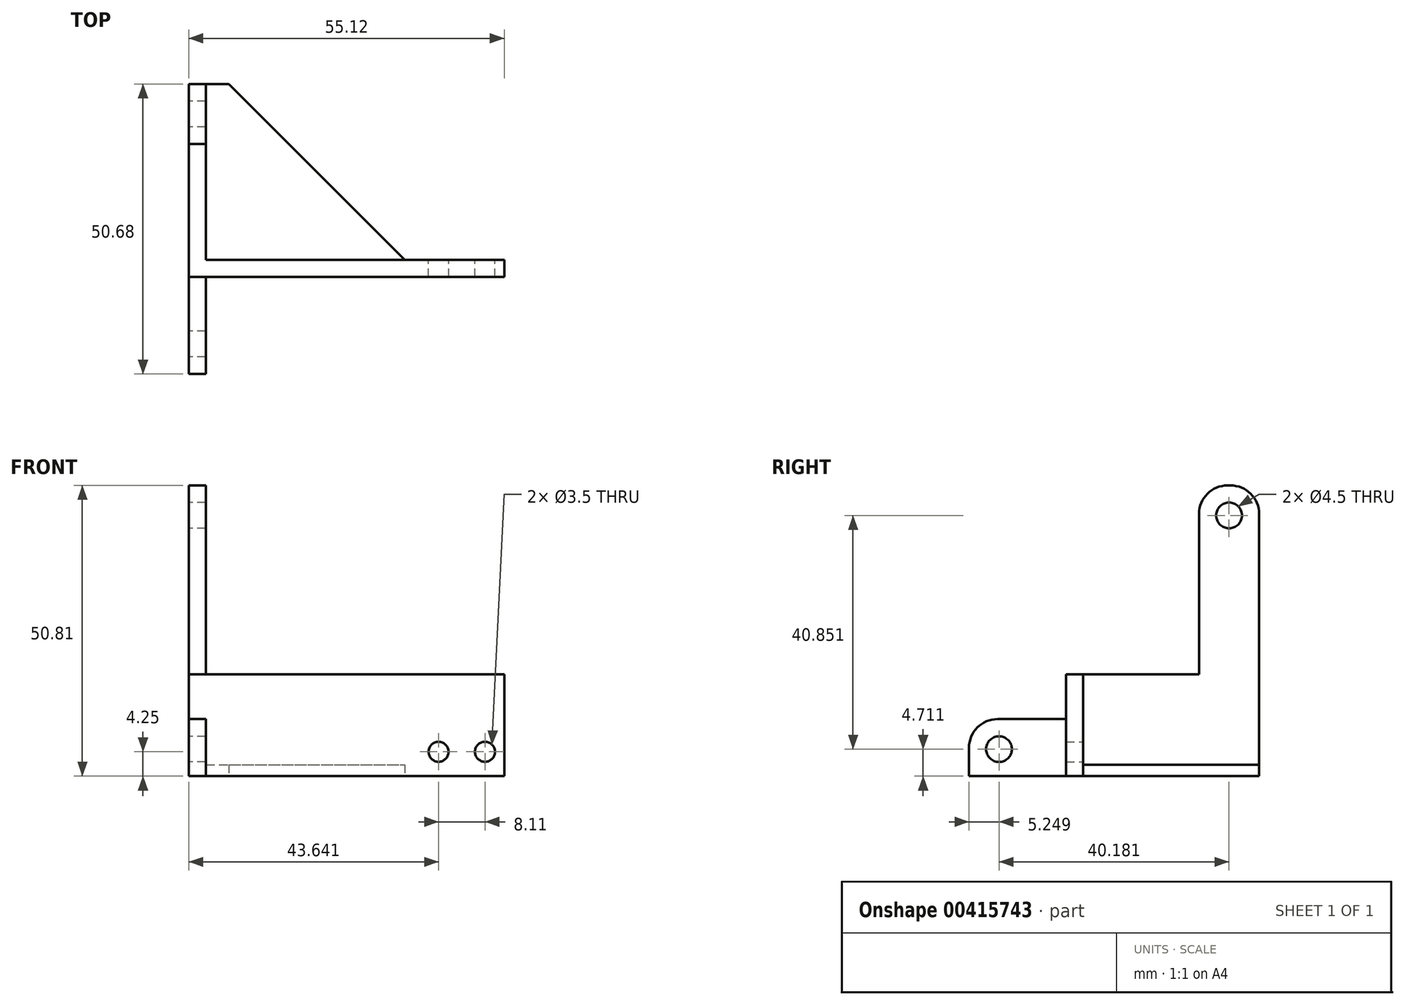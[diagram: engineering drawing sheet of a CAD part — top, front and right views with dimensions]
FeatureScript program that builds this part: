
annotation { "Feature Type Name" : "Feature", "Feature Type Description" : "" }
export const myFeature = defineFeature(function(context is Context, id is Id, definition is map)
    precondition{}
    {
        {
            var Q0;
            Q0=qCreatedBy(makeId("Front.planeOp"),FACE);
            var sketch = newSketch(context, id + "F0", { "sketchPlane" : qUnion([Q0])});
            skLineSegment(sketch, "E0.bottom", {"start": v(-7.56, 8.88) * mm, "end": v(7.56, 8.88) * mm});
            skLineSegment(sketch, "E0.top", {"start": v(-7.56, -8.88) * mm, "end": v(7.56, -8.88) * mm});
            skLineSegment(sketch, "E0.left", {"start": v(-7.56, 8.88) * mm, "end": v(-7.56, -8.88) * mm});
            skLineSegment(sketch, "E0.right", {"start": v(7.56, 8.88) * mm, "end": v(7.56, -8.88) * mm});
            skCircle(sketch, "E1", {"center": v(-3.92, -4.63) * mm, "radius": 1.75 * mm});
            skCircle(sketch, "E2", {"center": v(4.2, -4.63) * mm, "radius": 1.75 * mm});
            skLineSegment(sketch, "E3.bottom", {"start": v(-7.56, 8.88) * mm, "end": v(-47.56, 8.88) * mm});
            skLineSegment(sketch, "E3.top", {"start": v(-7.56, -8.88) * mm, "end": v(-47.56, -8.88) * mm});
            skLineSegment(sketch, "E3.right", {"start": v(-47.56, 8.88) * mm, "end": v(-47.56, -8.88) * mm});
            skLineSegment(sketch, "E4", {"start": v(-44.56, 8.88) * mm, "end": v(-44.56, -8.88) * mm});
            skLineSegment(sketch, "E5", {"start": v(-47.56, -6.88) * mm, "end": v(-9.56, -6.88) * mm});
            skLineSegment(sketch, "E6", {"start": v(-9.56, -6.88) * mm, "end": v(-9.56, -8.88) * mm});
            skSolve(sketch);
        }
        {
            var Q0;
            Q0=makeQuery(id+"F0.imprint","IMPRINT",FACE,{"disambiguationData":[TD([[makeQuery(id+"F0.imprint","IMPRINT",EDGE,{"derivedFrom":sQuery(id+"F0.wireOp",EDGE,"E0.bottom")}),-1.0]])]});
            var Q1;
            Q1=makeQuery(id+"F0.imprint","IMPRINT",FACE,{"disambiguationData":[TD([[makeQuery(id+"F0.imprint","IMPRINT",EDGE,{"derivedFrom":sQuery(id+"F0.wireOp",EDGE,"E3.bottom")}),1.0]])]});
            var Q2;
            {var subQ5=sQuery(id+"F0.wireOp",EDGE,"E0.left");Q2=makeQuery(id+"F0.imprint","IMPRINT",FACE,{"disambiguationData":[TD([[makeQuery(id+"F0.imprint","IMPRINT",EDGE,{"derivedFrom":subQ5}),-1.0]])]});}
            var Q3;
            {var subQ3=sQuery(id+"F0.wireOp",EDGE,"E6");Q3=makeQuery(id+"F0.imprint","IMPRINT",FACE,{"disambiguationData":[TD([[makeQuery(id+"F0.imprint","IMPRINT",EDGE,{"derivedFrom":subQ3}),-1.0]])]});}
            var Q4;
            {var subQ0=sQuery(id+"F0.wireOp",EDGE,"E3.right");var subQ1=sQuery(id+"F0.wireOp",EDGE,"E3.top");var subQ2=makeQuery(id+"F0.imprint","INTERSECT",VERTEX,{"derivedFrom":[subQ1,subQ0]});Q4=makeQuery(id+"F0.imprint","IMPRINT",FACE,{"disambiguationData":[TD([[makeQuery(id+"F0.imprint","IMPRINT",EDGE,{"disambiguationData":[TD([[subQ2,1.0]])],"derivedFrom":subQ1}),-1.0]])]});}
            extrude(context, id + "F1", {"entities" : qUnion([Q0, Q1, Q2, Q3, Q4]), "depth" : 3 * mm});
        }
        {
            var Q0;
            {var subQ0=sQuery(id+"F0.wireOp",EDGE,"E3.right");Q0=makeQuery(id+"F0.imprint","IMPRINT",FACE,{"disambiguationData":[TD([[makeQuery(id+"F0.imprint","IMPRINT",EDGE,{"derivedFrom":subQ0}),1.0]])]});}
            var Q1;
            {var subQ3=sQuery(id+"F0.wireOp",EDGE,"E6");Q1=makeQuery(id+"F0.imprint","IMPRINT",FACE,{"disambiguationData":[TD([[makeQuery(id+"F0.imprint","IMPRINT",EDGE,{"derivedFrom":subQ3}),-1.0]])]});}
            extrude(context, id + "F2", {"entities" : qUnion([Q0, Q1]), "operationType" : NewBodyOperationType.ADD, "oppositeDirection" : true, "depth" : 30.75 * mm});
        }
        {
            var Q0;
            {var subQ0=sQuery(id+"F0.wireOp",EDGE,"E3.right");Q0=makeQuery(id+"F2.boolean.opBoolean","MERGE",FACE,{"derivedFrom":[makeQuery(id+"F1.opExtrude","SWEPT_FACE",FACE,{"disambiguationData":[OSD([subQ0])]}),makeQuery(id+"F2.opExtrude","SWEPT_FACE",FACE,{"disambiguationData":[OSD([subQ0])]})]});}
            var sketch = newSketch(context, id + "F3", { "sketchPlane" : qUnion([Q0])});
            skLineSegment(sketch, "E7.bottom", {"start": v(-30.75, -8.88) * mm, "end": v(-20.25, -8.88) * mm});
            skLineSegment(sketch, "E7.top", {"start": v(-30.75, 34.42) * mm, "end": v(-20.25, 34.42) * mm});
            skLineSegment(sketch, "E7.left", {"start": v(-30.75, -8.88) * mm, "end": v(-30.75, 34.42) * mm});
            skLineSegment(sketch, "E7.right", {"start": v(-20.25, -8.88) * mm, "end": v(-20.25, 34.42) * mm});
            skCircle(sketch, "E8", {"center": v(-25.5, 36.68) * mm, "radius": 2.25 * mm});
            skLineSegment(sketch, "E9", {"start": v(-30.75, 34.42) * mm, "end": v(-30.75, 36.93) * mm});
            skLineSegment(sketch, "E10", {"start": v(-20.25, 34.42) * mm, "end": v(-20.25, 36.93) * mm});
            skLineSegment(sketch, "E11", {"start": v(-25.75, 41.93) * mm, "end": v(-25.25, 41.93) * mm});
            skPoint(sketch, "E12.visualSharp", {"position": v(-30.75, 41.93) * mm});
            skArc(sketch, "E12.filletArc", {"start": v(-25.75, 41.93) * mm, "mid": v(-29.29, 40.47) * mm, "end": v(-30.75, 36.93) * mm});
            skPoint(sketch, "E13.visualSharp", {"position": v(-20.25, 41.93) * mm});
            skArc(sketch, "E13.filletArc", {"start": v(-20.25, 36.93) * mm, "mid": v(-21.71, 40.47) * mm, "end": v(-25.25, 41.93) * mm});
            skLineSegment(sketch, "E14", {"start": v(-23.28, 37.02) * mm, "end": v(-23.28, 34.42) * mm});
            skLineSegment(sketch, "E15", {"start": v(-25.5, 36.68) * mm, "end": v(19.56, -9.13) * mm});
            skCircle(sketch, "E16", {"center": v(14.68, -4.17) * mm, "radius": 2.25 * mm});
            skLineSegment(sketch, "E17", {"start": v(3, -8.88) * mm, "end": v(19.93, -8.88) * mm});
            skLineSegment(sketch, "E18", {"start": v(19.93, -8.88) * mm, "end": v(19.93, -3.92) * mm});
            skLineSegment(sketch, "E19", {"start": v(14.93, 1.08) * mm, "end": v(3, 1.08) * mm});
            skPoint(sketch, "E20.visualSharp", {"position": v(19.93, 1.08) * mm});
            skArc(sketch, "E20.filletArc", {"start": v(19.93, -3.92) * mm, "mid": v(18.47, -0.38) * mm, "end": v(14.93, 1.08) * mm});
            skSolve(sketch);
        }
        {
            var Q0;
            Q0=makeQuery(id+"F3.imprint","IMPRINT",FACE,{"disambiguationData":[TD([[makeQuery(id+"F3.imprint","IMPRINT",EDGE,{"derivedFrom":sQuery(id+"F3.wireOp",EDGE,"E7.top")}),1.0]])]});
            var Q1;
            {var subQ0=sQuery(id+"F3.wireOp",EDGE,"E7.top");Q1=makeQuery(id+"F3.imprint","IMPRINT",FACE,{"disambiguationData":[TD([[makeQuery(id+"F3.imprint","IMPRINT",EDGE,{"derivedFrom":subQ0}),-1.0]])]});}
            var Q2;
            {var subQ0=sQuery(id+"F3.wireOp",EDGE,"E15");var subQ3=sQuery(id+"F3.wireOp",EDGE,"E7.right");var subQ4=makeQuery(id+"F3.imprint","INTERSECT",VERTEX,{"derivedFrom":[subQ3,subQ0]});Q2=makeQuery(id+"F3.imprint","IMPRINT",FACE,{"disambiguationData":[TD([[makeQuery(id+"F3.imprint","IMPRINT",EDGE,{"disambiguationData":[TD([[subQ4,1.0]])],"derivedFrom":subQ0}),-1.0]])]});}
            var Q3;
            {var subQ1=sQuery(id+"F3.wireOp",EDGE,"E15");var subQ10=sQuery(id+"F3.wireOp",EDGE,"E19");var subQ11=makeQuery(id+"F3.imprint","INTERSECT",VERTEX,{"derivedFrom":[subQ1,subQ10]});Q3=makeQuery(id+"F3.imprint","IMPRINT",FACE,{"disambiguationData":[TD([[makeQuery(id+"F3.imprint","IMPRINT",EDGE,{"disambiguationData":[TD([[subQ11,-1.0]])],"derivedFrom":subQ1}),-1.0]])]});}
            var Q4;
            {var subQ0=sQuery(id+"F3.wireOp",EDGE,"E18");Q4=makeQuery(id+"F3.imprint","IMPRINT",FACE,{"disambiguationData":[TD([[makeQuery(id+"F3.imprint","IMPRINT",EDGE,{"derivedFrom":subQ0}),1.0]])]});}
            var Q5;
            {var subQ0=sQuery(id+"F3.wireOp",EDGE,"E15");var subQ1=sQuery(id+"F3.wireOp",EDGE,"E8");var subQ2=makeQuery(id+"F3.imprint","INTERSECT",VERTEX,{"derivedFrom":[subQ1,subQ0]});Q5=makeQuery(id+"F3.imprint","IMPRINT",FACE,{"disambiguationData":[TD([[makeQuery(id+"F3.imprint","IMPRINT",EDGE,{"disambiguationData":[TD([[subQ2,-1.0]])],"derivedFrom":subQ1}),-1.0]])]});}
            extrude(context, id + "F4", {"entities" : qUnion([Q0, Q1, Q2, Q3, Q4, Q5]), "operationType" : NewBodyOperationType.ADD, "oppositeDirection" : true, "depth" : 3 * mm});
        }
        {
            var Q0;
            Q0=makeQuery(id+"F2.opExtrude","CAP_EDGE",EDGE,{"disambiguationData":[OSD([sQuery(id+"F0.wireOp",EDGE,"E6")])],"isStart":false});
            chamfer(context, id + "F5", {"entities" : qUnion([Q0]), "width" : 31 * mm, "tangentPropagation" : true});
        }
    });
